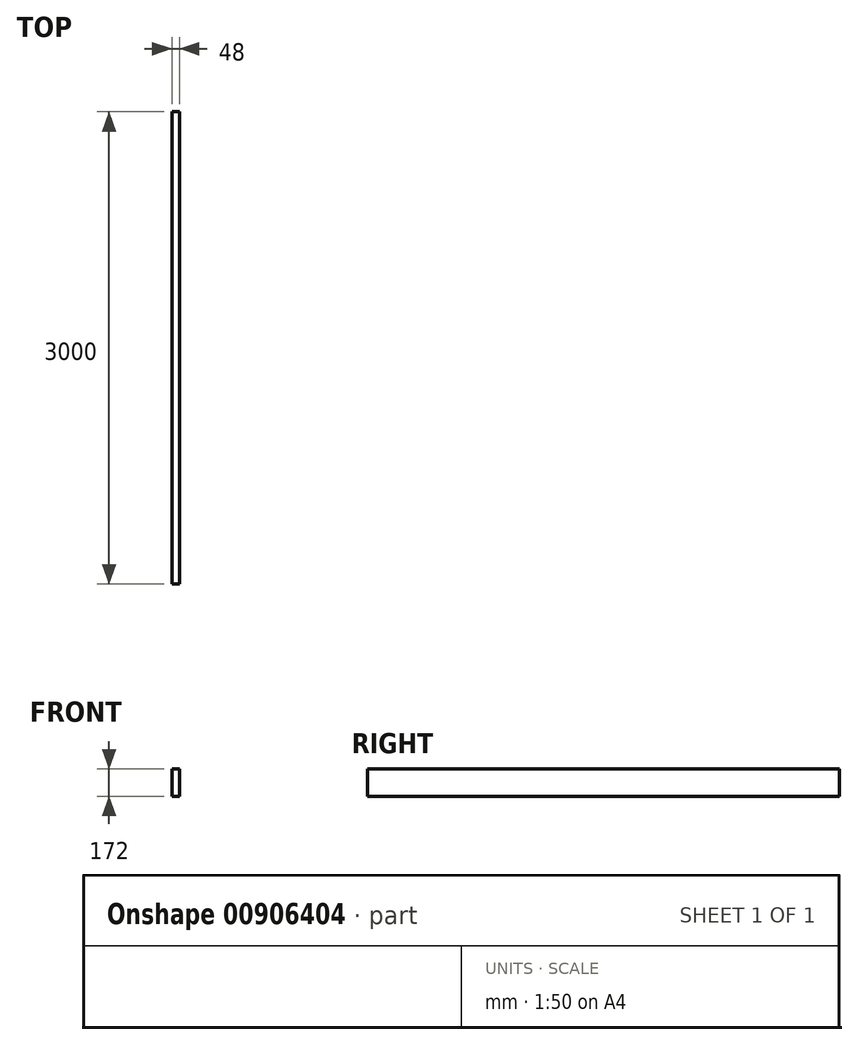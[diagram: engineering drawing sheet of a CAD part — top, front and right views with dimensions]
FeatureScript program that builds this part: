
annotation { "Feature Type Name" : "Feature", "Feature Type Description" : "" }
export const myFeature = defineFeature(function(context is Context, id is Id, definition is map)
    precondition{}
    {
        {
            var Q0;
            Q0=qCreatedBy(makeId("Front.planeOp"),FACE);
            var sketch = newSketch(context, id + "F0", { "sketchPlane" : qUnion([Q0])});
            skLineSegment(sketch, "E0.bottom", {"start": v(0, 0) * mm, "end": v(-48, 0) * mm});
            skLineSegment(sketch, "E0.top", {"start": v(0, -172) * mm, "end": v(-48, -172) * mm});
            skLineSegment(sketch, "E0.left", {"start": v(0, 0) * mm, "end": v(0, -172) * mm});
            skLineSegment(sketch, "E0.right", {"start": v(-48, 0) * mm, "end": v(-48, -172) * mm});
            skSolve(sketch);
        }
        {
            var Q0;
            Q0 = qSketchRegion(id + "F0", true);
            extrude(context, id + "F1", {"entities" : qUnion([Q0]), "depth" : 3000 * mm, "offsetDistance" : 25 * mm});
        }
    });
